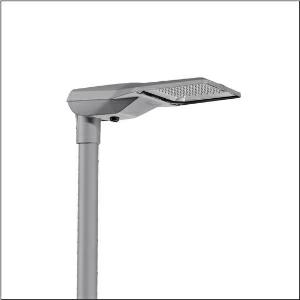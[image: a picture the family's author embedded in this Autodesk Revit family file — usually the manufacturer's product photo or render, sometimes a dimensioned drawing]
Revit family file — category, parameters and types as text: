
# Revit family: streetlight_sl_21_iq_midi___st1_0a_5xe3d31u08mb_cc74
name_source: partatom
category: Lighting Fixtures
units: mm (PartAtom-declared; Revit-internal decimal feet)

## family parameters
Cut with Voids When Loaded = No
Host = Face
Light Source = No
Part Type = Normal
Room Calculation Point = No
Round Connector Dimension = Use Diameter
Shared = No

## types (1)
- --- (1 x LED, 18340 lm, 129.3 W, 3000K)
    Apparent Load = 129 VA
    CIE Flux Codes = 37 72 97 100 100
    Color Rendering = 70
    Color Temperature = 3000K
    Default Elevation = 1800 mm
    Description = Streetlight SL 21 iQ midi, mast luminaire, primary light control with lens, of PMMA, primary optical cover: cover, of toughened safety glass, transparent, light distribution: ST1.0a, light emission: direct distribution, primary light characteristic: asymmetric, installation type: post-top, side-entry, LED, High Power LED, rated luminous flux: 18.340lm, luminous efficacy: 142lm/W, light colour: 730, colour temperature: 3000K, control: presetting dimming logarithmic, Street-Remote, Auto-Match, Temp-Guard, Lumen-Switch, Night-Set, Smart-Wire, Light-Fading, Desk-Remote (wireless, voltage-free reading and setting of iQ features in the workshop via application-optimized NFC function/RFID function), optimised constant luminous flux control (CLO 2.0), mains connection: 230..240V, AC, 50/60Hz, start of lifetime: 129W, end of service life: 142W, reduction: 56W, luminaire housing, of diecast aluminium, powder-coated, Siteco® metallic grey (DB 702S), corrosivity category C5 mid according to DIN EN ISO 12944, please order mast flange separately, inclination adjustable: 0°, 5°, 10°, 15°, sealing non-destructively replaceable, multi-level sealing system, length: 644mm, width: 335mm, height: 110mm, mast flange for spigot size: 42mm (side-entry): 5XC10008XM4, 60/48mm (side-entry/post-top): 5XC10108XM2, 76/60mm (side-entry/post-top): 5XC10108XM1, Smart Interface below, protection rating (complete): IP66, insulation class (complete): insulation class II (safety insulation), certification: CE, ENEC, ENEC+, VDE, impact resistance: IK09, permissible operating ambient temperature for outdoor applications: -40..+50°C, standard-compliant lighting for roads and squares, packaging unit: 1 piece

Light Distribution: ST1.0a
    Height = 111 mm
    Lamp = 1 x LED
    Lamp Light Flux = 18340 lm
    Lamp Power = 129.3 W
    Lamp count = 1
    Length = 644 mm
    Luminous efficacy = 142 lm/W
    Manufacturer = Siteco
    ModVariant = No
    Model = 5XE3D31U08MB
    Number of Poles = 1
    OnlyDefault = Yes
    Power Factor = 1
    Product Name = Streetlight SL 21 iQ midi | ST1.0a
    Product group = mast luminaire | pylon top
    ProductGroupID = 6100
    Protection Class = Protection class II
    Protection Degree = IP 66
    RLX_Detail_Level = 1
    RLX_Emergency_Light_Flux = 0 lm
    RLX_Emergency_Type = 0
    RLX_Emergency_Type_DB = No
    RlxData = <blob elided: 90917 chars, md5=dc8bf6b5>
    Socket = socket
    Standby Power = 0 W
    System Light Flux = 18340 lm
    System Power = 129 W
    Type Comments = factory setting: luminous flux: 100 % | dim-lin: 254 | 672 mA
    Type Image = l_1004300.jpg
    URL = http://relux.com
    VarID = @adj_044721
    Voltage = 0 V
    Weight = 0.00 kg
    Width = 336 mm

## geometry (parser evidence)
native form markers: Blend x4, Sweep x11
no freeform markers — native parametric forms only
